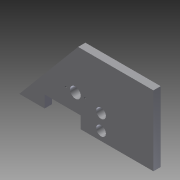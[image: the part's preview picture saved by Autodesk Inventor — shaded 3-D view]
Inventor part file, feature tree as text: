
AUTODESK INVENTOR PART (.ipt)
format: ipt  version: 2012 (Build 160160000, 160)  size: 161,280 bytes
history: native  units: in
note: dims shown in document units (in); Inventor stores cm internally (conversion verified against a paired STEP export)
features: other x4, sketch x1
ambient origin geometry x8: Origin, YZ Plane, XZ Plane, XY Plane, X Axis, Y Axis, Z Axis, Center Point
bodies: Solid1 (feature_tree)
feature tree (5):
  other  "Inside Chassis3.ipt"
  other  "Alias Freeform1"
  other  "Solid1::Inside Chassis3.ipt"
  sketch  "Sketch1"  dims[d0=0.3937in]
  other  "TaggingFeature1"
